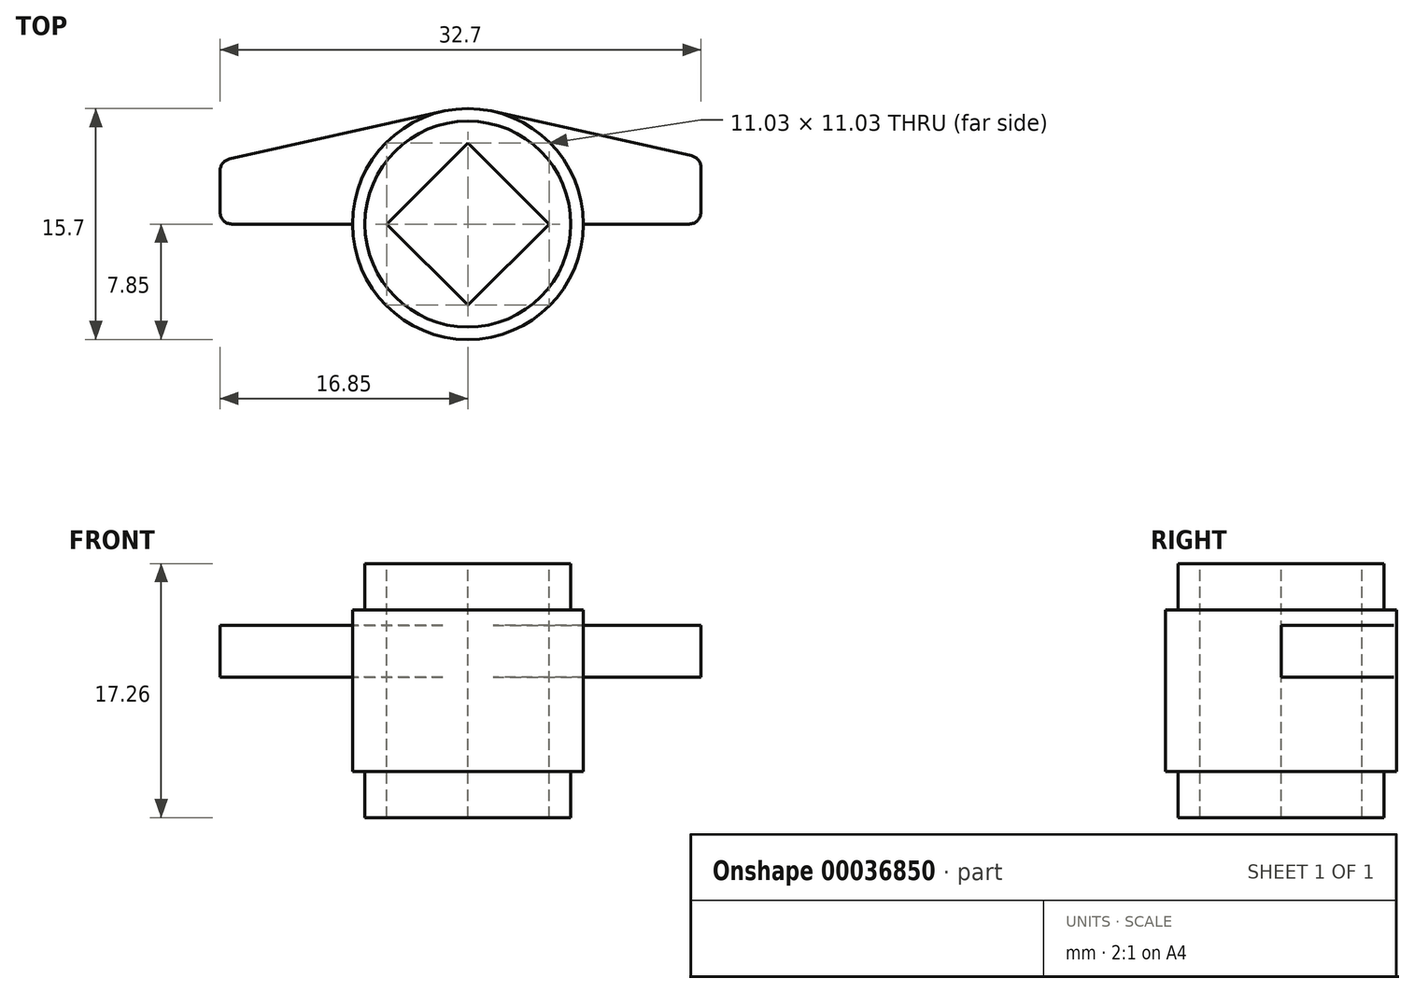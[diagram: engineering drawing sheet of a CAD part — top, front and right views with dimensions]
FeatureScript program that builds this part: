
annotation { "Feature Type Name" : "Feature", "Feature Type Description" : "" }
export const myFeature = defineFeature(function(context is Context, id is Id, definition is map)
    precondition{}
    {
        {
            var Q0;
            Q0=qCreatedBy(makeId("Top.planeOp"),FACE);
            var sketch = newSketch(context, id + "F0", { "sketchPlane" : qUnion([Q0])});
            skCircle(sketch, "E0", {"center": v(0, 0) * mm, "radius": 7.85 * mm});
            skLineSegment(sketch, "E1.bottom", {"start": v(-23.5, 27.4) * mm, "end": v(-9.5, 27.4) * mm});
            skLineSegment(sketch, "E1.top", {"start": v(-23.5, 3.4) * mm, "end": v(-9.5, 3.4) * mm});
            skLineSegment(sketch, "E1.left", {"start": v(-23.5, 27.4) * mm, "end": v(-23.5, 3.4) * mm});
            skLineSegment(sketch, "E1.right", {"start": v(-9.5, 27.4) * mm, "end": v(-9.5, 3.4) * mm});
            skLineSegment(sketch, "E2.bottom", {"start": v(-22.85, 11.82) * mm, "end": v(-17.94, 11.82) * mm});
            skLineSegment(sketch, "E2.top", {"start": v(-22.85, 12.85) * mm, "end": v(-17.94, 12.85) * mm});
            skLineSegment(sketch, "E2.left", {"start": v(-22.85, 11.82) * mm, "end": v(-22.85, 12.85) * mm});
            skLineSegment(sketch, "E2.right", {"start": v(-17.94, 11.82) * mm, "end": v(-17.94, 12.85) * mm});
            skCircle(sketch, "E3", {"center": v(-21.33, 6.62) * mm, "radius": 2.31 * mm});
            skSolve(sketch);
        }
        {
            var Q0;
            Q0=makeQuery(id+"F0.imprint","IMPRINT",FACE,{"disambiguationData":[TD([[makeQuery(id+"F0.imprint","IMPRINT",EDGE,{"derivedFrom":sQuery(id+"F0.wireOp",EDGE,"E0")}),1.0]])]});
            extrude(context, id + "F1", {"entities" : qUnion([Q0]), "depth" : 11 * mm});
        }
        {
            var Q0;
            Q0=makeQuery(id+"F1.opExtrude","CAP_FACE",FACE,{"disambiguationData":[OSD([sQuery(id+"F0.wireOp",EDGE,"E0")])],"isStart":false});
            var sketch = newSketch(context, id + "F2", { "sketchPlane" : qUnion([Q0])});
            skCircle(sketch, "E4", {"center": v(0, 0) * mm, "radius": 7 * mm});
            skSolve(sketch);
        }
        {
            var Q0;
            Q0 = qSketchRegion(id + "F2", true);
            extrude(context, id + "F3", {"entities" : qUnion([Q0]), "operationType" : NewBodyOperationType.ADD, "depth" : 3.13 * mm});
        }
        {
            var Q0;
            Q0=makeQuery(id+"F1.opExtrude","CAP_FACE",FACE,{"disambiguationData":[OSD([sQuery(id+"F0.wireOp",EDGE,"E0")])],"isStart":true});
            var sketch = newSketch(context, id + "F4", { "sketchPlane" : qUnion([Q0])});
            skCircle(sketch, "E5", {"center": v(0, 0) * mm, "radius": 7 * mm});
            skSolve(sketch);
        }
        {
            var Q0;
            Q0 = qSketchRegion(id + "F4", true);
            extrude(context, id + "F5", {"entities" : qUnion([Q0]), "operationType" : NewBodyOperationType.ADD, "depth" : 3.13 * mm});
        }
        {
            var Q0;
            Q0=makeQuery(id+"F3.opExtrude","CAP_FACE",FACE,{"disambiguationData":[OSD([sQuery(id+"F2.wireOp",EDGE,"E4")])],"isStart":false});
            var sketch = newSketch(context, id + "F6", { "sketchPlane" : qUnion([Q0])});
            skLineSegment(sketch, "E6", {"start": v(0, 5.52) * mm, "end": v(0, -5.52) * mm});
            skLineSegment(sketch, "E7", {"start": v(-5.52, 0) * mm, "end": v(5.52, 0) * mm});
            skLineSegment(sketch, "E8", {"start": v(-5.52, 0) * mm, "end": v(0, 5.52) * mm});
            skLineSegment(sketch, "E9", {"start": v(0, 5.52) * mm, "end": v(5.52, 0) * mm});
            skLineSegment(sketch, "E10", {"start": v(5.52, 0) * mm, "end": v(0, -5.52) * mm});
            skLineSegment(sketch, "E11", {"start": v(0, -5.52) * mm, "end": v(-5.52, 0) * mm});
            skSolve(sketch);
        }
        {
            var Q0;
            Q0 = qSketchRegion(id + "F6", true);
            extrude(context, id + "F7", {"entities" : qUnion([Q0]), "operationType" : NewBodyOperationType.REMOVE, "endBound" : BoundingType.THROUGH_ALL, "oppositeDirection" : true, "depth" : 25 * mm});
        }
        {
            var Q0;
            Q0=makeQuery(id+"F3.opExtrude","CAP_FACE",FACE,{"disambiguationData":[OSD([sQuery(id+"F2.wireOp",EDGE,"E4")])],"isStart":false});
            cPlane(context, id + "F8", {"entities" : qUnion([Q0]), "cplaneType" : CPlaneType.OFFSET, "offset" : 4.2 * mm, "oppositeDirection" : true, "width" : 150 * mm, "height" : 150 * mm});
        }
        {
            var Q0;
            Q0=qCreatedBy(id+"F8.planeOp",FACE);
            var sketch = newSketch(context, id + "F9", { "sketchPlane" : qUnion([Q0])});
            skLineSegment(sketch, "E12", {"start": v(-7.85, 0) * mm, "end": v(-16.05, 0) * mm});
            skLineSegment(sketch, "E13", {"start": v(-16.85, 0.8) * mm, "end": v(-16.85, 3.64) * mm});
            skLineSegment(sketch, "E14", {"start": v(-16.22, 4.42) * mm, "end": v(-1.71, 7.66) * mm});
            skLineSegment(sketch, "E15", {"start": v(1.71, 7.66) * mm, "end": v(15.22, 4.64) * mm});
            skLineSegment(sketch, "E16", {"start": v(15.85, 3.86) * mm, "end": v(15.85, 0.8) * mm});
            skLineSegment(sketch, "E17", {"start": v(15.05, 0) * mm, "end": v(7.85, 0) * mm});
            skPoint(sketch, "E18.visualSharp", {"position": v(-16.85, 0) * mm});
            skArc(sketch, "E18.filletArc", {"start": v(-16.85, 0.8) * mm, "mid": v(-16.62, 0.23) * mm, "end": v(-16.05, 0) * mm});
            skPoint(sketch, "E19.visualSharp", {"position": v(15.85, 0) * mm});
            skArc(sketch, "E19.filletArc", {"start": v(15.05, 0) * mm, "mid": v(15.62, 0.23) * mm, "end": v(15.85, 0.8) * mm});
            skPoint(sketch, "E20.visualSharp", {"position": v(15.85, 4.5) * mm});
            skArc(sketch, "E20.filletArc", {"start": v(15.85, 3.86) * mm, "mid": v(15.67, 4.36) * mm, "end": v(15.22, 4.64) * mm});
            skPoint(sketch, "E21.visualSharp", {"position": v(-16.85, 4.28) * mm});
            skArc(sketch, "E21.filletArc", {"start": v(-16.22, 4.42) * mm, "mid": v(-16.67, 4.14) * mm, "end": v(-16.85, 3.64) * mm});
            skArc(sketch, "E22", {"start": v(-1.71, 7.66) * mm, "mid": v(0, -7.85) * mm, "end": v(1.71, 7.66) * mm});
            skSolve(sketch);
        }
        {
            var Q0;
            Q0 = qSketchRegion(id + "F9", true);
            extrude(context, id + "F10", {"entities" : qUnion([Q0]), "operationType" : NewBodyOperationType.ADD, "oppositeDirection" : true, "depth" : 3.5 * mm});
        }
    });
